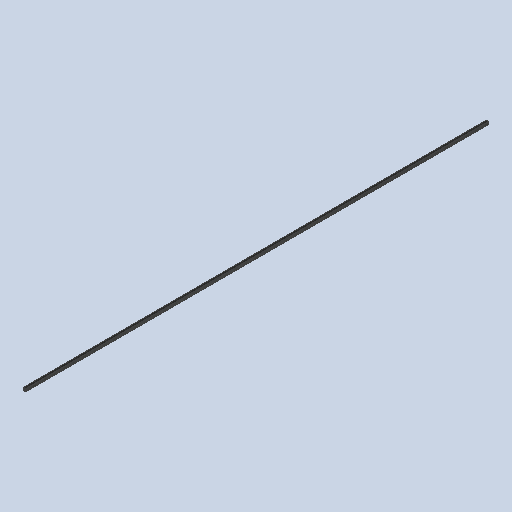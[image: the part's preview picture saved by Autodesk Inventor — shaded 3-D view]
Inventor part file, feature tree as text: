
AUTODESK INVENTOR PART (.ipt)
format: ipt  version: 2025 (Build 290162010, 162A)  size: 105,472 bytes
history: native  units: mm
features: other x1, extrude x1, sketch x1
ambient origin geometry x8: Origin, YZ Plane, XZ Plane, XY Plane, X Axis, Y Axis, Z Axis, Center Point
bodies: Solid1 (feature_tree)
feature tree (3):
  other  "BSH 064 tube 4"
  extrude  "Extrusion1"  Depth=6.0mm
  sketch  "Sketch1"  dims[d0=6.0mm d1=50.0mm d2=50.0mm d3=2.0mm d6=6.0mm d7=100.0mm d8=100.0mm d9=3.0mm d10=8080.0mm d11=0.0mm]
